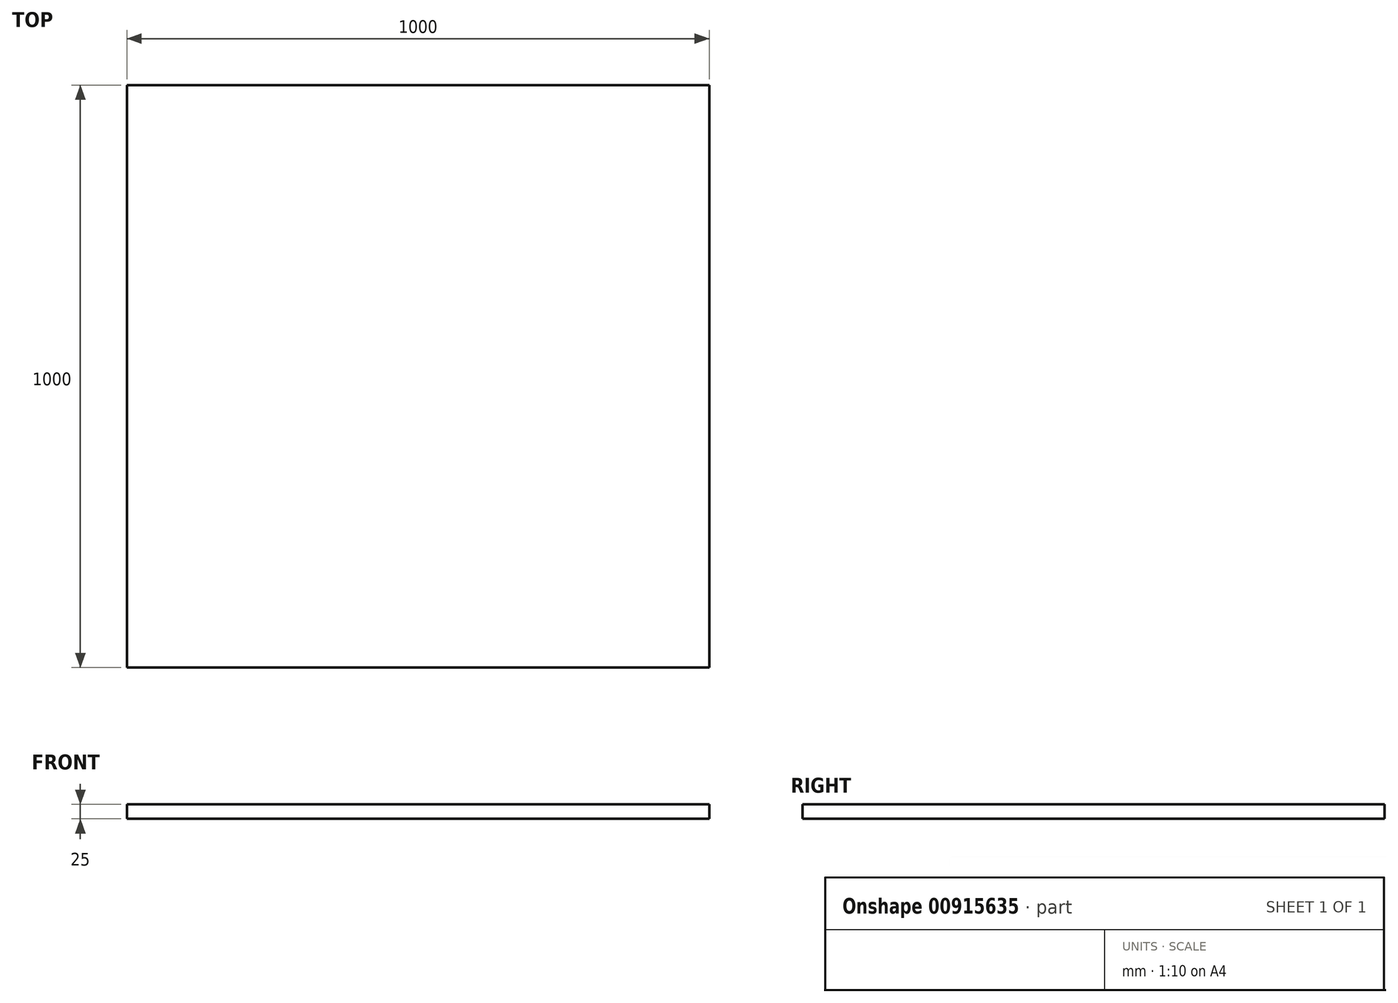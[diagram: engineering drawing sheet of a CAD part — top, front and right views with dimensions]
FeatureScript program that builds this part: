
annotation { "Feature Type Name" : "Feature", "Feature Type Description" : "" }
export const myFeature = defineFeature(function(context is Context, id is Id, definition is map)
    precondition{}
    {
        {
            var Q0;
            Q0=qCreatedBy(makeId("Top.planeOp"),FACE);
            var sketch = newSketch(context, id + "F0", { "sketchPlane" : qUnion([Q0])});
            skLineSegment(sketch, "E0.bottom", {"start": v(305, -305) * mm, "end": v(-305, -305) * mm});
            skLineSegment(sketch, "E0.top", {"start": v(305, 305) * mm, "end": v(-305, 305) * mm});
            skLineSegment(sketch, "E0.left", {"start": v(305, -305) * mm, "end": v(305, 305) * mm});
            skLineSegment(sketch, "E0.right", {"start": v(-305, -305) * mm, "end": v(-305, 305) * mm});
            skPoint(sketch, "E0.middle", {"position": v(0, 0) * mm});
            skLineSegment(sketch, "E1.bottom", {"start": v(500, -500) * mm, "end": v(-500, -500) * mm});
            skLineSegment(sketch, "E1.top", {"start": v(500, 500) * mm, "end": v(-500, 500) * mm});
            skLineSegment(sketch, "E1.left", {"start": v(500, -500) * mm, "end": v(500, 500) * mm});
            skLineSegment(sketch, "E1.right", {"start": v(-500, -500) * mm, "end": v(-500, 500) * mm});
            skSolve(sketch);
        }
        {
            var Q0;
            Q0=makeQuery(id+"F0.imprint","IMPRINT",FACE,{"disambiguationData":[TD([[makeQuery(id+"F0.imprint","IMPRINT",EDGE,{"derivedFrom":sQuery(id+"F0.wireOp",EDGE,"E0.bottom")}),1.0]])]});
            var Q1;
            Q1=makeQuery(id+"F0.imprint","IMPRINT",FACE,{"disambiguationData":[TD([[makeQuery(id+"F0.imprint","IMPRINT",EDGE,{"derivedFrom":sQuery(id+"F0.wireOp",EDGE,"E0.bottom")}),-1.0]])]});
            extrude(context, id + "F1", {"entities" : qUnion([Q0, Q1]), "oppositeDirection" : true, "depth" : 25 * mm, "offsetDistance" : 25 * mm});
        }
    });
